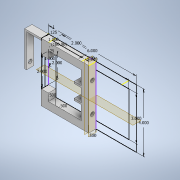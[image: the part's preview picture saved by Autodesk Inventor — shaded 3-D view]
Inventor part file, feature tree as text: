
AUTODESK INVENTOR PART (.ipt)
format: ipt  version: 2020 (Build 240168000, 168)  size: 262,656 bytes
history: native  units: in
note: dims shown in document units (in); Inventor stores cm internally (conversion verified against a paired STEP export)
features: sketch x7, extrude x5, hole x5, mirror x4, plane x3, split x1
ambient origin geometry x8: Origin, YZ Plane, XZ Plane, XY Plane, X Axis, Y Axis, Z Axis, Center Point
bodies: Solid1 (feature_tree)
feature tree (25):
  sketch  "Sketch1"  dims[d0=6.0in d1=4.0in]
  extrude  "Extrusion1"  Depth=4.0in
  sketch  "Sketch2"  dims[d2=0.5in d3=0.5in]
  extrude  "Extrusion2"  Depth=0.5in
  hole  "Hole1"  [1 undecoded]
  hole  "Hole2"  [1 undecoded]
  plane  "Work Plane1"
  plane  "Work Plane2"
  mirror  "Mirror1"
  mirror  "Mirror2"
  sketch  "Sketch5"  dims[d6=0.5in d7=0.5in d8=0.0in]
  hole  "Hole3"  [1 undecoded]
  extrude  "Extrusion3"  Depth=1.0in
  extrude  "Extrusion4"  TaperAngle=90.0deg  [1 undecoded]
  extrude  "Extrusion5"  Depth=1.0in
  hole  "Hole4"  [1 undecoded]
  mirror  "Mirror3"
  hole  "Hole5"  [1 undecoded]
  plane  "Work Plane3"
  split  "Split1"
  mirror  "Mirror4"
  sketch  "Sketch4"  dims[d4=5.0in d5=3.0in]
  sketch  "Sketch6"  dims[d9=2.0in]
  sketch  "Sketch7"  dims[d10=0.0725in d11=0.75in d12=0.375in d13=0.25in d14=0.5635in d15=3.5433in d16=0.0in d17=0.25in]
  sketch  "Sketch8"  dims[d18=0.135in d19=0.75in d20=0.375in d21=0.25in d22=0.5635in d23=0.125in d24=0.0in d25=1.0in d26=90.0deg d27=1.0in d28=180.0deg d29=0.125in d30=0.125in d31=0.5in d32=0.0in d33=1.0in d34=2.0in d35=1.0in d36=2.0in d37=180.0deg d38=0.266in d39=0.75in d40=0.507in d41=0.25in d42=0.5635in d43=1.0in d44=0.0in d45=0.125in d46=0.5in d47=0.0in d48=1.125in d49=0.0in d50=0.125in d51=2.25in d52=0.0in d53=0.25in d54=0.5in d55=0.266in d56=0.75in d57=0.507in d58=0.25in d59=0.5635in d60=1.0in d61=0.0in d62=0.125in d63=0.25in d64=180.0deg d65=0.5in d66=0.266in d67=0.75in d68=0.438in d69=0.25in d70=0.5635in d71=1.0in d72=0.0in d73=0.25in]
note: 6 required parameter values undecoded (feature->parameter linkage not recoverable at this tier; creation-order binding heuristic only, values carry confidence <= 0.55)
